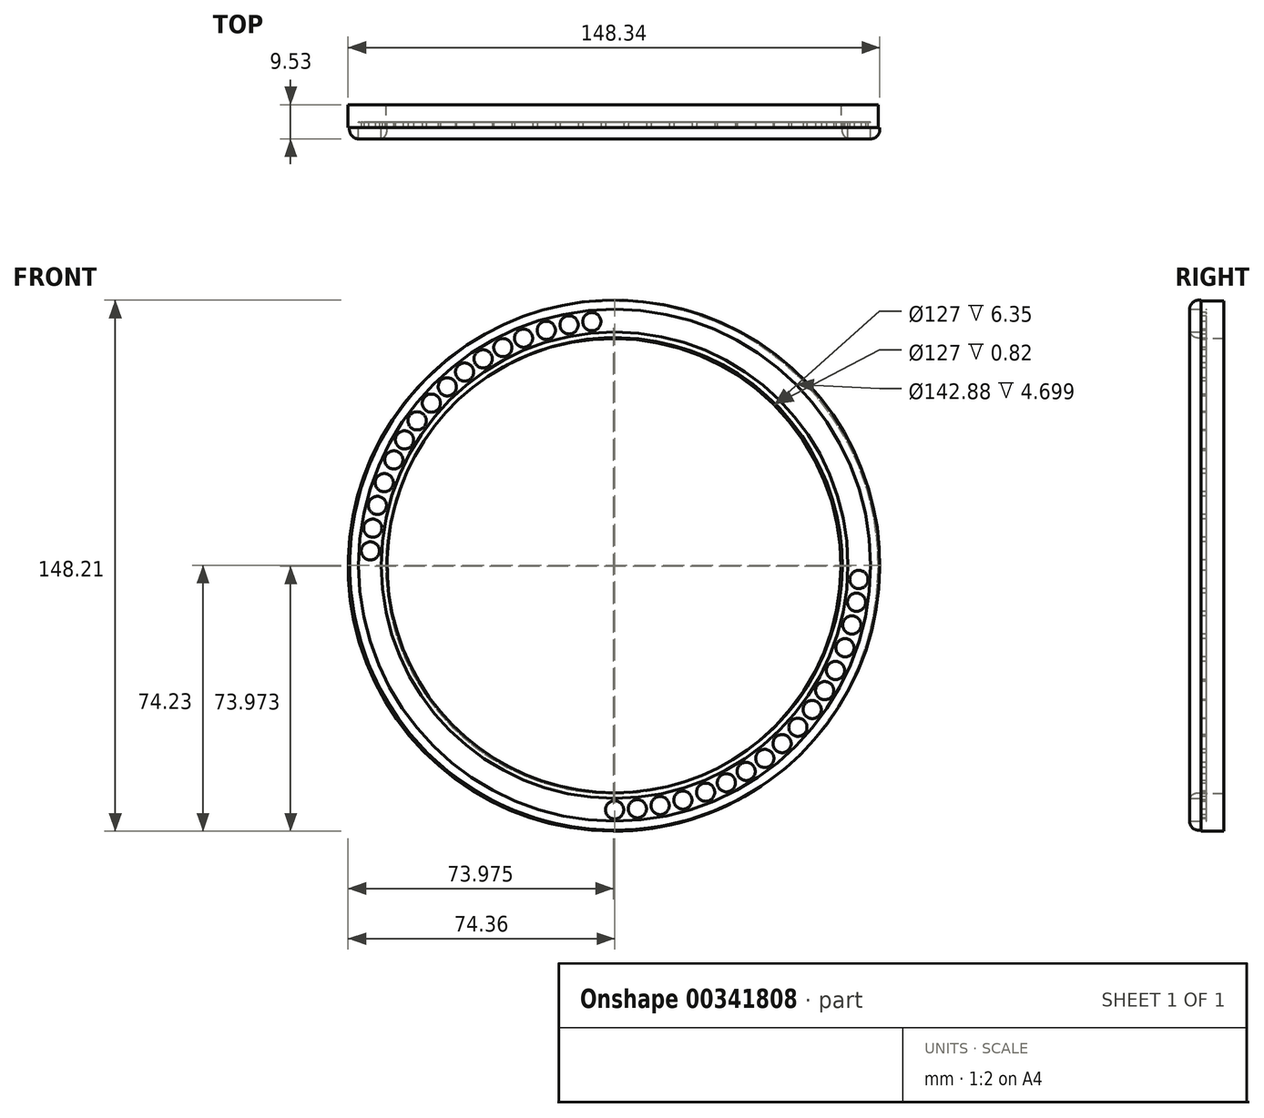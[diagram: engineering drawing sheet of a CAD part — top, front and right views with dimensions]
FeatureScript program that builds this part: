
annotation { "Feature Type Name" : "Feature", "Feature Type Description" : "" }
export const myFeature = defineFeature(function(context is Context, id is Id, definition is map)
    precondition{}
    {
        {
            var Q0;
            Q0=qCreatedBy(makeId("Front.planeOp"),FACE);
            var sketch = newSketch(context, id + "F0", { "sketchPlane" : qUnion([Q0])});
            skCircle(sketch, "E0", {"center": v(0, 0) * mm, "radius": 65.09 * mm});
            skCircle(sketch, "E1", {"center": v(0, 0) * mm, "radius": 71.44 * mm});
            skCircle(sketch, "E2", {"center": v(0, 0) * mm, "radius": 73.98 * mm});
            skCircle(sketch, "E3", {"center": v(0, 0) * mm, "radius": 63.5 * mm});
            skCircle(sketch, "E4", {"center": v(12.7, 67.07) * mm, "radius": 2.54 * mm});
            skCircle(sketch, "E5", {"center": v(19.05, 65.55) * mm, "radius": 2.54 * mm});
            skCircle(sketch, "E6", {"center": v(25.4, 63.36) * mm, "radius": 2.54 * mm});
            skCircle(sketch, "E7", {"center": v(31.18, 60.73) * mm, "radius": 2.54 * mm});
            skCircle(sketch, "E8", {"center": v(36.69, 57.57) * mm, "radius": 2.54 * mm});
            skCircle(sketch, "E9", {"center": v(41.88, 53.9) * mm, "radius": 2.54 * mm});
            skCircle(sketch, "E10", {"center": v(46.7, 49.78) * mm, "radius": 2.54 * mm});
            skCircle(sketch, "E11", {"center": v(51.13, 45.23) * mm, "radius": 2.54 * mm});
            skCircle(sketch, "E12", {"center": v(55.1, 40.28) * mm, "radius": 2.54 * mm});
            skCircle(sketch, "E13", {"center": v(58.61, 34.99) * mm, "radius": 2.54 * mm});
            skCircle(sketch, "E14", {"center": v(61.61, 29.39) * mm, "radius": 2.54 * mm});
            skCircle(sketch, "E15", {"center": v(64.26, 23.04) * mm, "radius": 2.54 * mm});
            skCircle(sketch, "E16", {"center": v(66.2, 16.69) * mm, "radius": 2.54 * mm});
            skCircle(sketch, "E17", {"center": v(67.47, 10.34) * mm, "radius": 2.54 * mm});
            skCircle(sketch, "E18", {"center": v(68.15, 3.99) * mm, "radius": 2.54 * mm});
            skCircle(sketch, "E19", {"center": v(6.35, 67.97) * mm, "radius": 2.54 * mm});
            skCircle(sketch, "E20", {"center": v(0, 68.26) * mm, "radius": 2.54 * mm});
            skCircle(sketch, "E21.MirrorC", {"center": v(-6.35, 67.97) * mm, "radius": 2.54 * mm});
            skCircle(sketch, "E22.MirrorC", {"center": v(-12.7, 67.07) * mm, "radius": 2.54 * mm});
            skCircle(sketch, "E23.MirrorC", {"center": v(-19.05, 65.55) * mm, "radius": 2.54 * mm});
            skCircle(sketch, "E24.MirrorC", {"center": v(-25.4, 63.36) * mm, "radius": 2.54 * mm});
            skCircle(sketch, "E25.MirrorC", {"center": v(-31.18, 60.73) * mm, "radius": 2.54 * mm});
            skCircle(sketch, "E26.MirrorC", {"center": v(-36.69, 57.57) * mm, "radius": 2.54 * mm});
            skCircle(sketch, "E27.MirrorC", {"center": v(-41.88, 53.9) * mm, "radius": 2.54 * mm});
            skCircle(sketch, "E28.MirrorC", {"center": v(-46.7, 49.78) * mm, "radius": 2.54 * mm});
            skCircle(sketch, "E29.MirrorC", {"center": v(-51.13, 45.23) * mm, "radius": 2.54 * mm});
            skCircle(sketch, "E30.MirrorC", {"center": v(-55.1, 40.28) * mm, "radius": 2.54 * mm});
            skCircle(sketch, "E31.MirrorC", {"center": v(-58.61, 34.99) * mm, "radius": 2.54 * mm});
            skCircle(sketch, "E32.MirrorC", {"center": v(-61.61, 29.39) * mm, "radius": 2.54 * mm});
            skCircle(sketch, "E33.MirrorC", {"center": v(-64.26, 23.04) * mm, "radius": 2.54 * mm});
            skCircle(sketch, "E34.MirrorC", {"center": v(-66.2, 16.69) * mm, "radius": 2.54 * mm});
            skCircle(sketch, "E35.MirrorC", {"center": v(-67.47, 10.34) * mm, "radius": 2.54 * mm});
            skCircle(sketch, "E36.MirrorC", {"center": v(-68.15, 3.99) * mm, "radius": 2.54 * mm});
            skCircle(sketch, "E37.MirrorC", {"center": v(68.15, -3.99) * mm, "radius": 2.54 * mm});
            skCircle(sketch, "E38.MirrorC", {"center": v(67.47, -10.34) * mm, "radius": 2.54 * mm});
            skCircle(sketch, "E39.MirrorC", {"center": v(66.2, -16.69) * mm, "radius": 2.54 * mm});
            skCircle(sketch, "E40.MirrorC", {"center": v(64.26, -23.04) * mm, "radius": 2.54 * mm});
            skCircle(sketch, "E41.MirrorC", {"center": v(61.61, -29.39) * mm, "radius": 2.54 * mm});
            skCircle(sketch, "E42.MirrorC", {"center": v(58.61, -34.99) * mm, "radius": 2.54 * mm});
            skCircle(sketch, "E43.MirrorC", {"center": v(55.1, -40.28) * mm, "radius": 2.54 * mm});
            skCircle(sketch, "E44.MirrorC", {"center": v(51.13, -45.23) * mm, "radius": 2.54 * mm});
            skCircle(sketch, "E45.MirrorC", {"center": v(46.7, -49.78) * mm, "radius": 2.54 * mm});
            skCircle(sketch, "E46.MirrorC", {"center": v(41.88, -53.9) * mm, "radius": 2.54 * mm});
            skCircle(sketch, "E47.MirrorC", {"center": v(36.69, -57.57) * mm, "radius": 2.54 * mm});
            skCircle(sketch, "E48.MirrorC", {"center": v(31.18, -60.73) * mm, "radius": 2.54 * mm});
            skCircle(sketch, "E49.MirrorC", {"center": v(25.4, -63.36) * mm, "radius": 2.54 * mm});
            skCircle(sketch, "E50.MirrorC", {"center": v(19.05, -65.55) * mm, "radius": 2.54 * mm});
            skCircle(sketch, "E51.MirrorC", {"center": v(12.7, -67.07) * mm, "radius": 2.54 * mm});
            skCircle(sketch, "E52.MirrorC", {"center": v(6.35, -67.97) * mm, "radius": 2.54 * mm});
            skCircle(sketch, "E53.MirrorC", {"center": v(0, -68.26) * mm, "radius": 2.54 * mm});
            skCircle(sketch, "E54.MirrorC", {"center": v(-6.35, -67.97) * mm, "radius": 2.54 * mm});
            skCircle(sketch, "E55.MirrorC", {"center": v(-12.7, -67.07) * mm, "radius": 2.54 * mm});
            skCircle(sketch, "E56.MirrorC", {"center": v(-19.05, -65.55) * mm, "radius": 2.54 * mm});
            skCircle(sketch, "E57.MirrorC", {"center": v(-25.4, -63.36) * mm, "radius": 2.54 * mm});
            skCircle(sketch, "E58.MirrorC", {"center": v(-31.18, -60.73) * mm, "radius": 2.54 * mm});
            skCircle(sketch, "E59.MirrorC", {"center": v(-36.69, -57.57) * mm, "radius": 2.54 * mm});
            skCircle(sketch, "E60.MirrorC", {"center": v(-41.88, -53.9) * mm, "radius": 2.54 * mm});
            skCircle(sketch, "E61.MirrorC", {"center": v(-46.7, -49.78) * mm, "radius": 2.54 * mm});
            skCircle(sketch, "E62.MirrorC", {"center": v(-51.13, -45.23) * mm, "radius": 2.54 * mm});
            skCircle(sketch, "E63.MirrorC", {"center": v(-55.1, -40.28) * mm, "radius": 2.54 * mm});
            skCircle(sketch, "E64.MirrorC", {"center": v(-58.61, -34.99) * mm, "radius": 2.54 * mm});
            skCircle(sketch, "E65.MirrorC", {"center": v(-61.61, -29.39) * mm, "radius": 2.54 * mm});
            skCircle(sketch, "E66.MirrorC", {"center": v(-64.26, -23.04) * mm, "radius": 2.54 * mm});
            skCircle(sketch, "E67.MirrorC", {"center": v(-66.2, -16.69) * mm, "radius": 2.54 * mm});
            skCircle(sketch, "E68.MirrorC", {"center": v(-67.47, -10.34) * mm, "radius": 2.54 * mm});
            skCircle(sketch, "E69.MirrorC", {"center": v(-68.15, -3.99) * mm, "radius": 2.54 * mm});
            skSolve(sketch);
        }
        {
            var Q0;
            Q0=qCreatedBy(makeId("Front.planeOp"),FACE);
            var sketch = newSketch(context, id + "F1", { "sketchPlane" : qUnion([Q0])});
            skCircle(sketch, "E70", {"center": v(-0.39, -0.26) * mm, "radius": 73.98 * mm});
            skCircle(sketch, "E71", {"center": v(-0.39, -0.26) * mm, "radius": 63.5 * mm});
            skSolve(sketch);
        }
        {
            var Q0;
            Q0=makeQuery(id+"F1.imprint","IMPRINT",FACE,{"disambiguationData":[TD([[makeQuery(id+"F1.imprint","IMPRINT",EDGE,{"derivedFrom":sQuery(id+"F1.wireOp",EDGE,"E70")}),1.0]])]});
            extrude(context, id + "F2", {"entities" : qUnion([Q0]), "oppositeDirection" : true, "depth" : 6.35 * mm, "offsetDistance" : 25.4 * mm});
        }
        {
            var Q0;
            Q0=makeQuery(id+"F0.imprint","IMPRINT",FACE,{"disambiguationData":[TD([[makeQuery(id+"F0.imprint","IMPRINT",EDGE,{"derivedFrom":sQuery(id+"F0.wireOp",EDGE,"E1")}),-1.0]])]});
            var Q1;
            Q1=makeQuery(id+"F0.imprint","IMPRINT",FACE,{"disambiguationData":[TD([[makeQuery(id+"F0.imprint","IMPRINT",EDGE,{"derivedFrom":sQuery(id+"F0.wireOp",EDGE,"E0")}),1.0]])]});
            extrude(context, id + "F3", {"entities" : qUnion([Q0, Q1]), "operationType" : NewBodyOperationType.ADD, "depth" : 3.17 * mm, "offsetDistance" : 25.4 * mm});
        }
        {
            var Q0;
            Q0=makeQuery(id+"F0.imprint","IMPRINT",FACE,{"disambiguationData":[TD([[makeQuery(id+"F0.imprint","IMPRINT",EDGE,{"derivedFrom":sQuery(id+"F0.wireOp",EDGE,"E35.MirrorC")}),-1.0]])]});
            var Q1;
            Q1=makeQuery(id+"F0.imprint","IMPRINT",FACE,{"disambiguationData":[TD([[makeQuery(id+"F0.imprint","IMPRINT",EDGE,{"derivedFrom":sQuery(id+"F0.wireOp",EDGE,"E34.MirrorC")}),-1.0]])]});
            var Q2;
            Q2=makeQuery(id+"F0.imprint","IMPRINT",FACE,{"disambiguationData":[TD([[makeQuery(id+"F0.imprint","IMPRINT",EDGE,{"derivedFrom":sQuery(id+"F0.wireOp",EDGE,"E33.MirrorC")}),-1.0]])]});
            var Q3;
            Q3=makeQuery(id+"F0.imprint","IMPRINT",FACE,{"disambiguationData":[TD([[makeQuery(id+"F0.imprint","IMPRINT",EDGE,{"derivedFrom":sQuery(id+"F0.wireOp",EDGE,"E32.MirrorC")}),-1.0]])]});
            var Q4;
            Q4=makeQuery(id+"F0.imprint","IMPRINT",FACE,{"disambiguationData":[TD([[makeQuery(id+"F0.imprint","IMPRINT",EDGE,{"derivedFrom":sQuery(id+"F0.wireOp",EDGE,"E31.MirrorC")}),-1.0]])]});
            var Q5;
            Q5=makeQuery(id+"F0.imprint","IMPRINT",FACE,{"disambiguationData":[TD([[makeQuery(id+"F0.imprint","IMPRINT",EDGE,{"derivedFrom":sQuery(id+"F0.wireOp",EDGE,"E30.MirrorC")}),-1.0]])]});
            var Q6;
            Q6=makeQuery(id+"F0.imprint","IMPRINT",FACE,{"disambiguationData":[TD([[makeQuery(id+"F0.imprint","IMPRINT",EDGE,{"derivedFrom":sQuery(id+"F0.wireOp",EDGE,"E29.MirrorC")}),-1.0]])]});
            var Q7;
            Q7=makeQuery(id+"F0.imprint","IMPRINT",FACE,{"disambiguationData":[TD([[makeQuery(id+"F0.imprint","IMPRINT",EDGE,{"derivedFrom":sQuery(id+"F0.wireOp",EDGE,"E28.MirrorC")}),-1.0]])]});
            var Q8;
            Q8=makeQuery(id+"F0.imprint","IMPRINT",FACE,{"disambiguationData":[TD([[makeQuery(id+"F0.imprint","IMPRINT",EDGE,{"derivedFrom":sQuery(id+"F0.wireOp",EDGE,"E27.MirrorC")}),-1.0]])]});
            var Q9;
            Q9=makeQuery(id+"F0.imprint","IMPRINT",FACE,{"disambiguationData":[TD([[makeQuery(id+"F0.imprint","IMPRINT",EDGE,{"derivedFrom":sQuery(id+"F0.wireOp",EDGE,"E26.MirrorC")}),-1.0]])]});
            var Q10;
            Q10=makeQuery(id+"F0.imprint","IMPRINT",FACE,{"disambiguationData":[TD([[makeQuery(id+"F0.imprint","IMPRINT",EDGE,{"derivedFrom":sQuery(id+"F0.wireOp",EDGE,"E25.MirrorC")}),-1.0]])]});
            var Q11;
            Q11=makeQuery(id+"F0.imprint","IMPRINT",FACE,{"disambiguationData":[TD([[makeQuery(id+"F0.imprint","IMPRINT",EDGE,{"derivedFrom":sQuery(id+"F0.wireOp",EDGE,"E24.MirrorC")}),-1.0]])]});
            var Q12;
            Q12=makeQuery(id+"F0.imprint","IMPRINT",FACE,{"disambiguationData":[TD([[makeQuery(id+"F0.imprint","IMPRINT",EDGE,{"derivedFrom":sQuery(id+"F0.wireOp",EDGE,"E23.MirrorC")}),-1.0]])]});
            var Q13;
            Q13=makeQuery(id+"F0.imprint","IMPRINT",FACE,{"disambiguationData":[TD([[makeQuery(id+"F0.imprint","IMPRINT",EDGE,{"derivedFrom":sQuery(id+"F0.wireOp",EDGE,"E22.MirrorC")}),-1.0]])]});
            var Q14;
            Q14=makeQuery(id+"F0.imprint","IMPRINT",FACE,{"disambiguationData":[TD([[makeQuery(id+"F0.imprint","IMPRINT",EDGE,{"derivedFrom":sQuery(id+"F0.wireOp",EDGE,"E21.MirrorC")}),-1.0]])]});
            var Q15;
            Q15=makeQuery(id+"F0.imprint","IMPRINT",FACE,{"disambiguationData":[TD([[makeQuery(id+"F0.imprint","IMPRINT",EDGE,{"derivedFrom":sQuery(id+"F0.wireOp",EDGE,"E20")}),1.0]])]});
            var Q16;
            Q16=makeQuery(id+"F0.imprint","IMPRINT",FACE,{"disambiguationData":[TD([[makeQuery(id+"F0.imprint","IMPRINT",EDGE,{"derivedFrom":sQuery(id+"F0.wireOp",EDGE,"E19")}),1.0]])]});
            var Q17;
            Q17=makeQuery(id+"F0.imprint","IMPRINT",FACE,{"disambiguationData":[TD([[makeQuery(id+"F0.imprint","IMPRINT",EDGE,{"derivedFrom":sQuery(id+"F0.wireOp",EDGE,"E4")}),1.0]])]});
            var Q18;
            Q18=makeQuery(id+"F0.imprint","IMPRINT",FACE,{"disambiguationData":[TD([[makeQuery(id+"F0.imprint","IMPRINT",EDGE,{"derivedFrom":sQuery(id+"F0.wireOp",EDGE,"E5")}),1.0]])]});
            var Q19;
            Q19=makeQuery(id+"F0.imprint","IMPRINT",FACE,{"disambiguationData":[TD([[makeQuery(id+"F0.imprint","IMPRINT",EDGE,{"derivedFrom":sQuery(id+"F0.wireOp",EDGE,"E6")}),1.0]])]});
            var Q20;
            Q20=makeQuery(id+"F0.imprint","IMPRINT",FACE,{"disambiguationData":[TD([[makeQuery(id+"F0.imprint","IMPRINT",EDGE,{"derivedFrom":sQuery(id+"F0.wireOp",EDGE,"E7")}),1.0]])]});
            var Q21;
            Q21=makeQuery(id+"F0.imprint","IMPRINT",FACE,{"disambiguationData":[TD([[makeQuery(id+"F0.imprint","IMPRINT",EDGE,{"derivedFrom":sQuery(id+"F0.wireOp",EDGE,"E8")}),1.0]])]});
            var Q22;
            Q22=makeQuery(id+"F0.imprint","IMPRINT",FACE,{"disambiguationData":[TD([[makeQuery(id+"F0.imprint","IMPRINT",EDGE,{"derivedFrom":sQuery(id+"F0.wireOp",EDGE,"E9")}),1.0]])]});
            var Q23;
            Q23=makeQuery(id+"F0.imprint","IMPRINT",FACE,{"disambiguationData":[TD([[makeQuery(id+"F0.imprint","IMPRINT",EDGE,{"derivedFrom":sQuery(id+"F0.wireOp",EDGE,"E10")}),1.0]])]});
            var Q24;
            Q24=makeQuery(id+"F0.imprint","IMPRINT",FACE,{"disambiguationData":[TD([[makeQuery(id+"F0.imprint","IMPRINT",EDGE,{"derivedFrom":sQuery(id+"F0.wireOp",EDGE,"E11")}),1.0]])]});
            var Q25;
            Q25=makeQuery(id+"F0.imprint","IMPRINT",FACE,{"disambiguationData":[TD([[makeQuery(id+"F0.imprint","IMPRINT",EDGE,{"derivedFrom":sQuery(id+"F0.wireOp",EDGE,"E12")}),1.0]])]});
            var Q26;
            Q26=makeQuery(id+"F0.imprint","IMPRINT",FACE,{"disambiguationData":[TD([[makeQuery(id+"F0.imprint","IMPRINT",EDGE,{"derivedFrom":sQuery(id+"F0.wireOp",EDGE,"E13")}),1.0]])]});
            var Q27;
            Q27=makeQuery(id+"F0.imprint","IMPRINT",FACE,{"disambiguationData":[TD([[makeQuery(id+"F0.imprint","IMPRINT",EDGE,{"derivedFrom":sQuery(id+"F0.wireOp",EDGE,"E14")}),1.0]])]});
            var Q28;
            Q28=makeQuery(id+"F0.imprint","IMPRINT",FACE,{"disambiguationData":[TD([[makeQuery(id+"F0.imprint","IMPRINT",EDGE,{"derivedFrom":sQuery(id+"F0.wireOp",EDGE,"E15")}),1.0]])]});
            var Q29;
            Q29=makeQuery(id+"F0.imprint","IMPRINT",FACE,{"disambiguationData":[TD([[makeQuery(id+"F0.imprint","IMPRINT",EDGE,{"derivedFrom":sQuery(id+"F0.wireOp",EDGE,"E16")}),1.0]])]});
            var Q30;
            Q30=makeQuery(id+"F0.imprint","IMPRINT",FACE,{"disambiguationData":[TD([[makeQuery(id+"F0.imprint","IMPRINT",EDGE,{"derivedFrom":sQuery(id+"F0.wireOp",EDGE,"E17")}),1.0]])]});
            var Q31;
            Q31=makeQuery(id+"F0.imprint","IMPRINT",FACE,{"disambiguationData":[TD([[makeQuery(id+"F0.imprint","IMPRINT",EDGE,{"derivedFrom":sQuery(id+"F0.wireOp",EDGE,"E18")}),1.0]])]});
            var Q32;
            Q32=makeQuery(id+"F0.imprint","IMPRINT",FACE,{"disambiguationData":[TD([[makeQuery(id+"F0.imprint","IMPRINT",EDGE,{"derivedFrom":sQuery(id+"F0.wireOp",EDGE,"E37.MirrorC")}),-1.0]])]});
            var Q33;
            Q33=makeQuery(id+"F0.imprint","IMPRINT",FACE,{"disambiguationData":[TD([[makeQuery(id+"F0.imprint","IMPRINT",EDGE,{"derivedFrom":sQuery(id+"F0.wireOp",EDGE,"E38.MirrorC")}),-1.0]])]});
            var Q34;
            Q34=makeQuery(id+"F0.imprint","IMPRINT",FACE,{"disambiguationData":[TD([[makeQuery(id+"F0.imprint","IMPRINT",EDGE,{"derivedFrom":sQuery(id+"F0.wireOp",EDGE,"E39.MirrorC")}),-1.0]])]});
            var Q35;
            Q35=makeQuery(id+"F0.imprint","IMPRINT",FACE,{"disambiguationData":[TD([[makeQuery(id+"F0.imprint","IMPRINT",EDGE,{"derivedFrom":sQuery(id+"F0.wireOp",EDGE,"E40.MirrorC")}),-1.0]])]});
            var Q36;
            Q36=makeQuery(id+"F0.imprint","IMPRINT",FACE,{"disambiguationData":[TD([[makeQuery(id+"F0.imprint","IMPRINT",EDGE,{"derivedFrom":sQuery(id+"F0.wireOp",EDGE,"E41.MirrorC")}),-1.0]])]});
            var Q37;
            Q37=makeQuery(id+"F0.imprint","IMPRINT",FACE,{"disambiguationData":[TD([[makeQuery(id+"F0.imprint","IMPRINT",EDGE,{"derivedFrom":sQuery(id+"F0.wireOp",EDGE,"E42.MirrorC")}),-1.0]])]});
            var Q38;
            Q38=makeQuery(id+"F0.imprint","IMPRINT",FACE,{"disambiguationData":[TD([[makeQuery(id+"F0.imprint","IMPRINT",EDGE,{"derivedFrom":sQuery(id+"F0.wireOp",EDGE,"E43.MirrorC")}),-1.0]])]});
            var Q39;
            Q39=makeQuery(id+"F0.imprint","IMPRINT",FACE,{"disambiguationData":[TD([[makeQuery(id+"F0.imprint","IMPRINT",EDGE,{"derivedFrom":sQuery(id+"F0.wireOp",EDGE,"E44.MirrorC")}),-1.0]])]});
            var Q40;
            Q40=makeQuery(id+"F0.imprint","IMPRINT",FACE,{"disambiguationData":[TD([[makeQuery(id+"F0.imprint","IMPRINT",EDGE,{"derivedFrom":sQuery(id+"F0.wireOp",EDGE,"E45.MirrorC")}),-1.0]])]});
            var Q41;
            Q41=makeQuery(id+"F0.imprint","IMPRINT",FACE,{"disambiguationData":[TD([[makeQuery(id+"F0.imprint","IMPRINT",EDGE,{"derivedFrom":sQuery(id+"F0.wireOp",EDGE,"E46.MirrorC")}),-1.0]])]});
            var Q42;
            Q42=makeQuery(id+"F0.imprint","IMPRINT",FACE,{"disambiguationData":[TD([[makeQuery(id+"F0.imprint","IMPRINT",EDGE,{"derivedFrom":sQuery(id+"F0.wireOp",EDGE,"E47.MirrorC")}),-1.0]])]});
            var Q43;
            Q43=makeQuery(id+"F0.imprint","IMPRINT",FACE,{"disambiguationData":[TD([[makeQuery(id+"F0.imprint","IMPRINT",EDGE,{"derivedFrom":sQuery(id+"F0.wireOp",EDGE,"E48.MirrorC")}),-1.0]])]});
            var Q44;
            Q44=makeQuery(id+"F0.imprint","IMPRINT",FACE,{"disambiguationData":[TD([[makeQuery(id+"F0.imprint","IMPRINT",EDGE,{"derivedFrom":sQuery(id+"F0.wireOp",EDGE,"E49.MirrorC")}),-1.0]])]});
            var Q45;
            Q45=makeQuery(id+"F0.imprint","IMPRINT",FACE,{"disambiguationData":[TD([[makeQuery(id+"F0.imprint","IMPRINT",EDGE,{"derivedFrom":sQuery(id+"F0.wireOp",EDGE,"E50.MirrorC")}),-1.0]])]});
            var Q46;
            Q46=makeQuery(id+"F0.imprint","IMPRINT",FACE,{"disambiguationData":[TD([[makeQuery(id+"F0.imprint","IMPRINT",EDGE,{"derivedFrom":sQuery(id+"F0.wireOp",EDGE,"E51.MirrorC")}),-1.0]])]});
            var Q47;
            Q47=makeQuery(id+"F0.imprint","IMPRINT",FACE,{"disambiguationData":[TD([[makeQuery(id+"F0.imprint","IMPRINT",EDGE,{"derivedFrom":sQuery(id+"F0.wireOp",EDGE,"E52.MirrorC")}),-1.0]])]});
            var Q48;
            Q48=makeQuery(id+"F0.imprint","IMPRINT",FACE,{"disambiguationData":[TD([[makeQuery(id+"F0.imprint","IMPRINT",EDGE,{"derivedFrom":sQuery(id+"F0.wireOp",EDGE,"E53.MirrorC")}),-1.0]])]});
            var Q49;
            Q49=makeQuery(id+"F0.imprint","IMPRINT",FACE,{"disambiguationData":[TD([[makeQuery(id+"F0.imprint","IMPRINT",EDGE,{"derivedFrom":sQuery(id+"F0.wireOp",EDGE,"E54.MirrorC")}),1.0]])]});
            var Q50;
            Q50=makeQuery(id+"F0.imprint","IMPRINT",FACE,{"disambiguationData":[TD([[makeQuery(id+"F0.imprint","IMPRINT",EDGE,{"derivedFrom":sQuery(id+"F0.wireOp",EDGE,"E55.MirrorC")}),1.0]])]});
            var Q51;
            Q51=makeQuery(id+"F0.imprint","IMPRINT",FACE,{"disambiguationData":[TD([[makeQuery(id+"F0.imprint","IMPRINT",EDGE,{"derivedFrom":sQuery(id+"F0.wireOp",EDGE,"E56.MirrorC")}),1.0]])]});
            var Q52;
            Q52=makeQuery(id+"F0.imprint","IMPRINT",FACE,{"disambiguationData":[TD([[makeQuery(id+"F0.imprint","IMPRINT",EDGE,{"derivedFrom":sQuery(id+"F0.wireOp",EDGE,"E57.MirrorC")}),1.0]])]});
            var Q53;
            Q53=makeQuery(id+"F0.imprint","IMPRINT",FACE,{"disambiguationData":[TD([[makeQuery(id+"F0.imprint","IMPRINT",EDGE,{"derivedFrom":sQuery(id+"F0.wireOp",EDGE,"E58.MirrorC")}),1.0]])]});
            var Q54;
            Q54=makeQuery(id+"F0.imprint","IMPRINT",FACE,{"disambiguationData":[TD([[makeQuery(id+"F0.imprint","IMPRINT",EDGE,{"derivedFrom":sQuery(id+"F0.wireOp",EDGE,"E59.MirrorC")}),1.0]])]});
            var Q55;
            Q55=makeQuery(id+"F0.imprint","IMPRINT",FACE,{"disambiguationData":[TD([[makeQuery(id+"F0.imprint","IMPRINT",EDGE,{"derivedFrom":sQuery(id+"F0.wireOp",EDGE,"E60.MirrorC")}),1.0]])]});
            var Q56;
            Q56=makeQuery(id+"F0.imprint","IMPRINT",FACE,{"disambiguationData":[TD([[makeQuery(id+"F0.imprint","IMPRINT",EDGE,{"derivedFrom":sQuery(id+"F0.wireOp",EDGE,"E61.MirrorC")}),1.0]])]});
            var Q57;
            Q57=makeQuery(id+"F0.imprint","IMPRINT",FACE,{"disambiguationData":[TD([[makeQuery(id+"F0.imprint","IMPRINT",EDGE,{"derivedFrom":sQuery(id+"F0.wireOp",EDGE,"E62.MirrorC")}),1.0]])]});
            var Q58;
            Q58=makeQuery(id+"F0.imprint","IMPRINT",FACE,{"disambiguationData":[TD([[makeQuery(id+"F0.imprint","IMPRINT",EDGE,{"derivedFrom":sQuery(id+"F0.wireOp",EDGE,"E63.MirrorC")}),1.0]])]});
            var Q59;
            Q59=makeQuery(id+"F0.imprint","IMPRINT",FACE,{"disambiguationData":[TD([[makeQuery(id+"F0.imprint","IMPRINT",EDGE,{"derivedFrom":sQuery(id+"F0.wireOp",EDGE,"E64.MirrorC")}),1.0]])]});
            var Q60;
            Q60=makeQuery(id+"F0.imprint","IMPRINT",FACE,{"disambiguationData":[TD([[makeQuery(id+"F0.imprint","IMPRINT",EDGE,{"derivedFrom":sQuery(id+"F0.wireOp",EDGE,"E65.MirrorC")}),1.0]])]});
            var Q61;
            Q61=makeQuery(id+"F0.imprint","IMPRINT",FACE,{"disambiguationData":[TD([[makeQuery(id+"F0.imprint","IMPRINT",EDGE,{"derivedFrom":sQuery(id+"F0.wireOp",EDGE,"E66.MirrorC")}),1.0]])]});
            var Q62;
            Q62=makeQuery(id+"F0.imprint","IMPRINT",FACE,{"disambiguationData":[TD([[makeQuery(id+"F0.imprint","IMPRINT",EDGE,{"derivedFrom":sQuery(id+"F0.wireOp",EDGE,"E67.MirrorC")}),1.0]])]});
            var Q63;
            Q63=makeQuery(id+"F0.imprint","IMPRINT",FACE,{"disambiguationData":[TD([[makeQuery(id+"F0.imprint","IMPRINT",EDGE,{"derivedFrom":sQuery(id+"F0.wireOp",EDGE,"E68.MirrorC")}),1.0]])]});
            var Q64;
            Q64=makeQuery(id+"F0.imprint","IMPRINT",FACE,{"disambiguationData":[TD([[makeQuery(id+"F0.imprint","IMPRINT",EDGE,{"derivedFrom":sQuery(id+"F0.wireOp",EDGE,"E69.MirrorC")}),1.0]])]});
            var Q65;
            Q65=makeQuery(id+"F0.imprint","IMPRINT",FACE,{"disambiguationData":[TD([[makeQuery(id+"F0.imprint","IMPRINT",EDGE,{"derivedFrom":sQuery(id+"F0.wireOp",EDGE,"E36.MirrorC")}),-1.0]])]});
            extrude(context, id + "F4", {"entities" : qUnion([Q0, Q1, Q2, Q3, Q4, Q5, Q6, Q7, Q8, Q9, Q10, Q11, Q12, Q13, Q14, Q15, Q16, Q17, Q18, Q19, Q20, Q21, Q22, Q23, Q24, Q25, Q26, Q27, Q28, Q29, Q30, Q31, Q32, Q33, Q34, Q35, Q36, Q37, Q38, Q39, Q40, Q41, Q42, Q43, Q44, Q45, Q46, Q47, Q48, Q49, Q50, Q51, Q52, Q53, Q54, Q55, Q56, Q57, Q58, Q59, Q60, Q61, Q62, Q63, Q64, Q65]), "operationType" : NewBodyOperationType.REMOVE, "oppositeDirection" : true, "depth" : 1.52 * mm, "offsetDistance" : 25.4 * mm});
        }
        {
            var Q0;
            Q0=makeQuery(id+"F3.opExtrude","CAP_EDGE",EDGE,{"disambiguationData":[OSD([sQuery(id+"F0.wireOp",EDGE,"E2")])],"isStart":false});
            var Q1;
            Q1=makeQuery(id+"F3.opExtrude","CAP_EDGE",EDGE,{"disambiguationData":[OSD([sQuery(id+"F0.wireOp",EDGE,"E3")])],"isStart":false});
            fillet(context, id + "F5", {"entities" : qUnion([Q0, Q1]), "tangentPropagation" : true, "radius" : 2.54 * mm, "defaultsChanged" : true, "vertexSettings" : [], "allowEdgeOverflow" : false});
        }
    });
